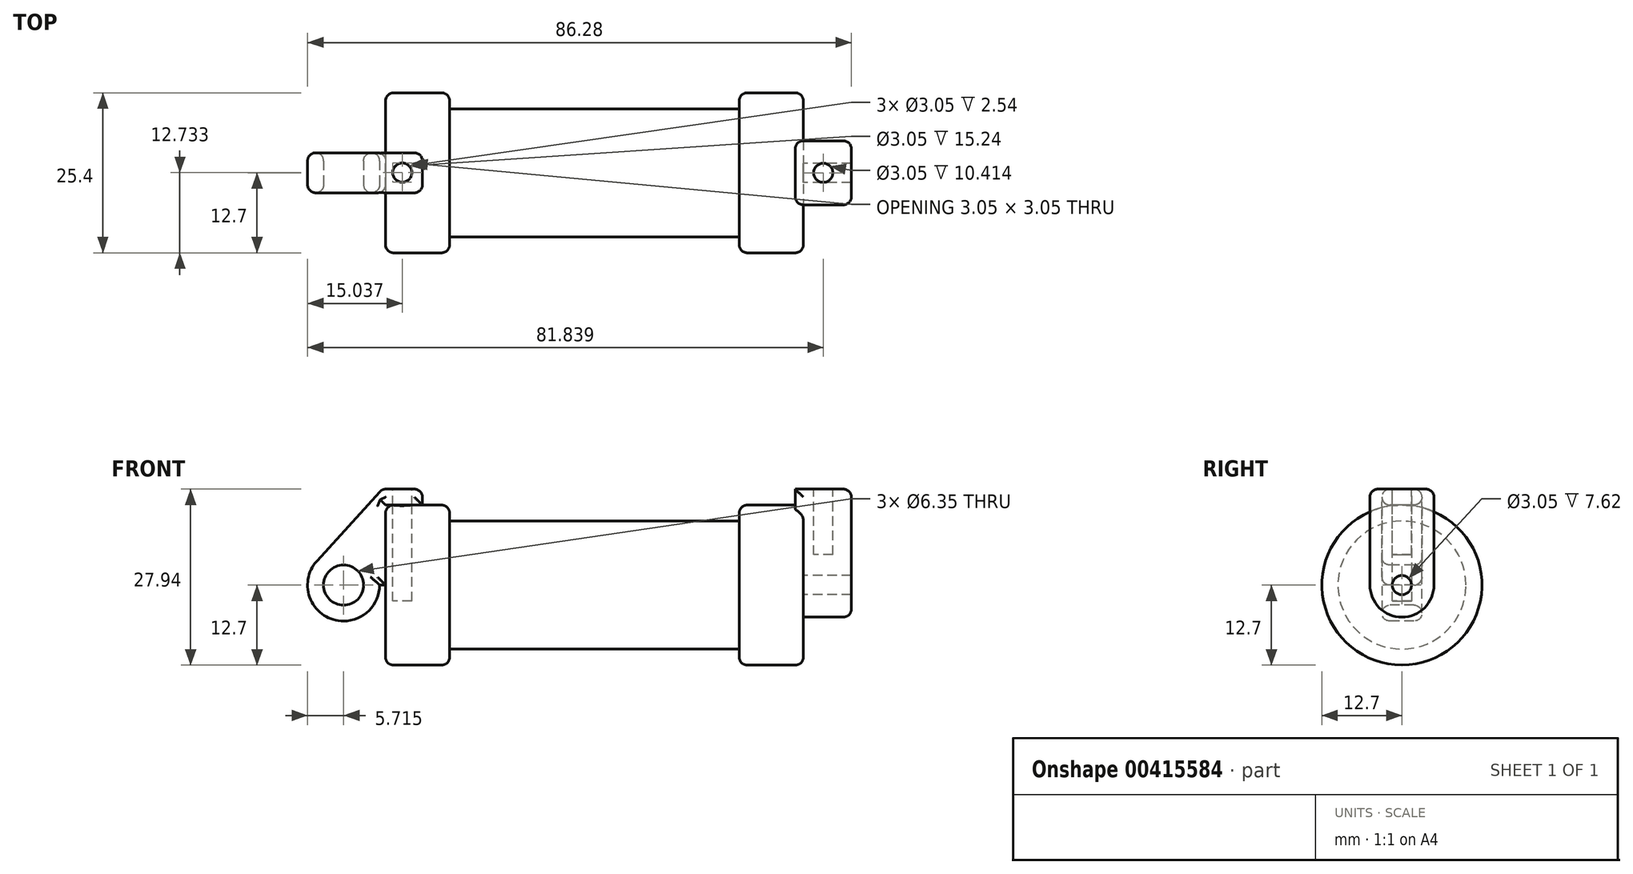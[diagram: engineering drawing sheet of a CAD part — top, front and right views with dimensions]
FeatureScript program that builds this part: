
annotation { "Feature Type Name" : "Feature", "Feature Type Description" : "" }
export const myFeature = defineFeature(function(context is Context, id is Id, definition is map)
    precondition{}
    {
        {
            var Q0;
            Q0=qCreatedBy(makeId("Front.planeOp"),FACE);
            var sketch = newSketch(context, id + "F0", { "sketchPlane" : qUnion([Q0])});
            skLineSegment(sketch, "E0", {"start": v(0, 0) * mm, "end": v(0, 12.7) * mm});
            skLineSegment(sketch, "E1", {"start": v(0, 12.7) * mm, "end": v(10.16, 12.7) * mm});
            skLineSegment(sketch, "E2", {"start": v(10.16, 12.7) * mm, "end": v(10.16, 10.16) * mm});
            skLineSegment(sketch, "E3", {"start": v(10.16, 10.16) * mm, "end": v(56.13, 10.16) * mm});
            skLineSegment(sketch, "E4", {"start": v(56.13, 10.16) * mm, "end": v(56.13, 12.7) * mm});
            skLineSegment(sketch, "E5", {"start": v(56.13, 12.7) * mm, "end": v(66.3, 12.7) * mm});
            skLineSegment(sketch, "E6", {"start": v(66.3, 12.7) * mm, "end": v(66.3, 0) * mm});
            skLineSegment(sketch, "E7", {"start": v(66.3, 0) * mm, "end": v(0, 0) * mm});
            skLineSegment(sketch, "E8", {"start": v(5.84, 15.24) * mm, "end": v(-0.5, 15.24) * mm});
            skLineSegment(sketch, "E9", {"start": v(-0.5, 15.24) * mm, "end": v(-10.88, 3.85) * mm});
            skLineSegment(sketch, "E10", {"start": v(0, 0) * mm, "end": v(-6.65, 0) * mm});
            skCircle(sketch, "E11", {"center": v(-6.65, 0) * mm, "radius": 5.72 * mm});
            skCircle(sketch, "E12", {"center": v(-6.65, 0) * mm, "radius": 3.18 * mm});
            skLineSegment(sketch, "E13", {"start": v(5.84, -9.4) * mm, "end": v(-8.18, -5.5) * mm});
            skLineSegment(sketch, "E14", {"start": v(5.84, 15.24) * mm, "end": v(5.84, 12.7) * mm});
            skSolve(sketch);
        }
        {
            var Q0;
            {var subQ3=sQuery(id+"F0.wireOp",EDGE,"E0");Q0=makeQuery(id+"F0.imprint","IMPRINT",FACE,{"disambiguationData":[TD([[makeQuery(id+"F0.imprint","IMPRINT",EDGE,{"derivedFrom":subQ3}),-1.0]])]});}
            var Q1;
            Q1=sQuery(id+"F0.wireOp",EDGE,"E7");
            revolve(context, id + "F1", {"entities" : qUnion([Q0]), "axis" : qUnion([Q1]), "revolveType" : RevolveType.FULL});
        }
        {
            var Q0;
            {var subQ5=sQuery(id+"F0.wireOp",EDGE,"E12");Q0=makeQuery(id+"F0.imprint","IMPRINT",FACE,{"disambiguationData":[TD([[makeQuery(id+"F0.imprint","IMPRINT",EDGE,{"derivedFrom":subQ5}),-1.0]])]});}
            var Q1;
            {var subQ1=sQuery(id+"F0.wireOp",EDGE,"E0");Q1=makeQuery(id+"F0.imprint","IMPRINT",FACE,{"disambiguationData":[TD([[makeQuery(id+"F0.imprint","IMPRINT",EDGE,{"derivedFrom":subQ1}),1.0]])]});}
            extrude(context, id + "F2", {"entities" : qUnion([Q0, Q1]), "endBound" : BoundingType.SYMMETRIC, "oppositeDirection" : true, "depth" : 6.35 * mm});
        }
        {
            var Q0;
            Q0=makeQuery(id+"F1.opRevolve","SWEPT_FACE",FACE,{"disambiguationData":[OSD([sQuery(id+"F0.wireOp",EDGE,"E6")])]});
            var sketch = newSketch(context, id + "F3", { "sketchPlane" : qUnion([Q0])});
            skCircle(sketch, "E15", {"center": v(0, 0) * mm, "radius": 1.52 * mm});
            skCircle(sketch, "E16", {"center": v(0, 0) * mm, "radius": 5.08 * mm});
            skLineSegment(sketch, "E17", {"start": v(-5.08, 0) * mm, "end": v(-5.08, 15.24) * mm});
            skLineSegment(sketch, "E18", {"start": v(5.08, 0) * mm, "end": v(5.08, 15.24) * mm});
            skLineSegment(sketch, "E19", {"start": v(-5.08, 15.24) * mm, "end": v(5.08, 15.24) * mm});
            skSolve(sketch);
        }
        {
            var Q0;
            {var subQ0=sQuery(id+"F3.wireOp",EDGE,"E19");Q0=makeQuery(id+"F3.imprint","IMPRINT",FACE,{"disambiguationData":[TD([[makeQuery(id+"F3.imprint","IMPRINT",EDGE,{"derivedFrom":subQ0}),-1.0]])]});}
            extrude(context, id + "F4", {"entities" : qUnion([Q0]), "operationType" : NewBodyOperationType.ADD, "oppositeDirection" : true, "depth" : 1.27 * mm});
        }
        {
            var Q0;
            {var subQ0=sQuery(id+"F3.wireOp",EDGE,"E17");var subQ1=sQuery(id+"F3.wireOp",EDGE,"E16");var subQ2=makeQuery(id+"F3.imprint","INTERSECT",VERTEX,{"derivedFrom":[subQ1,subQ0]});Q0=makeQuery(id+"F3.imprint","IMPRINT",FACE,{"disambiguationData":[TD([[makeQuery(id+"F3.imprint","IMPRINT",EDGE,{"disambiguationData":[TD([[subQ2,1.0]])],"derivedFrom":subQ1}),-1.0]])]});}
            var Q1;
            {var subQ0=sQuery(id+"F3.wireOp",EDGE,"E19");Q1=makeQuery(id+"F3.imprint","IMPRINT",FACE,{"disambiguationData":[TD([[makeQuery(id+"F3.imprint","IMPRINT",EDGE,{"derivedFrom":subQ0}),-1.0]])]});}
            var Q2;
            Q2=makeQuery(id+"F3.imprint","IMPRINT",FACE,{"disambiguationData":[TD([[makeQuery(id+"F3.imprint","IMPRINT",EDGE,{"derivedFrom":sQuery(id+"F3.wireOp",EDGE,"E15")}),-1.0]])]});
            extrude(context, id + "F5", {"entities" : qUnion([Q0, Q1, Q2]), "operationType" : NewBodyOperationType.ADD, "depth" : 7.62 * mm});
        }
        {
            var Q0;
            Q0=makeQuery(id+"F3.imprint","IMPRINT",FACE,{"disambiguationData":[TD([[makeQuery(id+"F3.imprint","IMPRINT",EDGE,{"derivedFrom":sQuery(id+"F3.wireOp",EDGE,"E15")}),1.0]])]});
            var Q1;
            Q1=makeQuery(id+"F1.opRevolve","SWEPT_FACE",FACE,{"disambiguationData":[OSD([sQuery(id+"F0.wireOp",EDGE,"E2")])]});
            extrude(context, id + "F6", {"entities" : qUnion([Q0]), "operationType" : NewBodyOperationType.ADD, "endBound" : BoundingType.UP_TO_SURFACE, "oppositeDirection" : true, "endBoundEntityFace" : qUnion([Q1]), "depth" : 64.77 * mm});
        }
        {
            var Q0;
            {var subQ0=sQuery(id+"F3.wireOp",EDGE,"E19");Q0=makeQuery(id+"F5.boolean.opBoolean","MERGE",FACE,{"derivedFrom":[makeQuery(id+"F4.opExtrude","SWEPT_FACE",FACE,{"disambiguationData":[OSD([subQ0])]}),makeQuery(id+"F5.opExtrude","SWEPT_FACE",FACE,{"disambiguationData":[OSD([subQ0])]})]});}
            var sketch = newSketch(context, id + "F7", { "sketchPlane" : qUnion([Q0])});
            skCircle(sketch, "E20", {"center": v(69.47, 0) * mm, "radius": 1.52 * mm});
            skLineSegment(sketch, "E21", {"start": v(69.47, 0) * mm, "end": v(73.91, 0) * mm, "construction": true});
            skLineSegment(sketch, "E22", {"start": v(69.47, 0) * mm, "end": v(69.47, 5.08) * mm, "construction": true});
            skSolve(sketch);
        }
        {
            var Q0;
            Q0=makeQuery(id+"F2.opExtrude","SWEPT_FACE",FACE,{"disambiguationData":[OSD([sQuery(id+"F0.wireOp",EDGE,"E8")])]});
            var sketch = newSketch(context, id + "F8", { "sketchPlane" : qUnion([Q0])});
            skCircle(sketch, "E23", {"center": v(2.67, 0.03) * mm, "radius": 1.52 * mm});
            skPoint(sketch, "E23.centerSnap0", {"position": v(2.67, 3.17) * mm});
            skSolve(sketch);
        }
        {
            var Q0;
            Q0=makeQuery(id+"F8.imprint","IMPRINT",FACE,{"disambiguationData":[TD([[makeQuery(id+"F8.imprint","IMPRINT",EDGE,{"derivedFrom":sQuery(id+"F8.wireOp",EDGE,"E23")}),1.0]])]});
            extrude(context, id + "F9", {"entities" : qUnion([Q0]), "operationType" : NewBodyOperationType.REMOVE, "oppositeDirection" : true, "depth" : 17.78 * mm});
        }
        {
            var Q0;
            Q0=makeQuery(id+"F7.imprint","IMPRINT",FACE,{"disambiguationData":[TD([[makeQuery(id+"F7.imprint","IMPRINT",EDGE,{"derivedFrom":sQuery(id+"F7.wireOp",EDGE,"E20")}),1.0]])]});
            extrude(context, id + "F10", {"entities" : qUnion([Q0]), "operationType" : NewBodyOperationType.REMOVE, "oppositeDirection" : true, "depth" : 10.4 * mm});
        }
        {
            var Q0;
            Q0=makeQuery(id+"F1.opRevolve","SWEPT_EDGE",EDGE,{"disambiguationData":[OSD([sQuery(id+"F0.wireOp",EDGE,"E5"),sQuery(id+"F0.wireOp",EDGE,"E6")])]});
            var Q1;
            Q1=makeQuery(id+"F1.opRevolve","SWEPT_EDGE",EDGE,{"disambiguationData":[OSD([sQuery(id+"F0.wireOp",EDGE,"E1"),sQuery(id+"F0.wireOp",EDGE,"E2")])]});
            var Q2;
            Q2=makeQuery(id+"F1.opRevolve","SWEPT_EDGE",EDGE,{"disambiguationData":[OSD([sQuery(id+"F0.wireOp",EDGE,"E0"),sQuery(id+"F0.wireOp",EDGE,"E1")])]});
            var Q3;
            Q3=makeQuery(id+"F1.opRevolve","SWEPT_EDGE",EDGE,{"disambiguationData":[OSD([sQuery(id+"F0.wireOp",EDGE,"E4"),sQuery(id+"F0.wireOp",EDGE,"E5")])]});
            fillet(context, id + "F11", {"entities" : qUnion([Q0, Q1, Q2, Q3]), "radius" : 1.27 * mm, "tangentPropagation" : true, "allowEdgeOverflow" : false});
        }
        {
            var Q0;
            Q0=makeQuery(id+"F5.opExtrude","CAP_EDGE",EDGE,{"disambiguationData":[OSD([sQuery(id+"F3.wireOp",EDGE,"E19")])],"isStart":false});
            var Q1;
            {var subQ0=sQuery(id+"F3.wireOp",EDGE,"E19");var subQ1=sQuery(id+"F3.wireOp",EDGE,"E17");Q1=makeQuery(id+"F5.boolean.opBoolean","MERGE",EDGE,{"derivedFrom":[makeQuery(id+"F4.opExtrude","SWEPT_EDGE",EDGE,{"disambiguationData":[OSD([subQ1,subQ0])]}),makeQuery(id+"F5.opExtrude","SWEPT_EDGE",EDGE,{"disambiguationData":[OSD([subQ1,subQ0])]})]});}
            var Q2;
            Q2=makeQuery(id+"F5.opExtrude","CAP_EDGE",EDGE,{"disambiguationData":[OSD([sQuery(id+"F3.wireOp",EDGE,"E18")])],"isStart":false});
            var Q3;
            Q3=makeQuery(id+"F4.opExtrude","CAP_EDGE",EDGE,{"disambiguationData":[OSD([sQuery(id+"F3.wireOp",EDGE,"E17")])],"isStart":false});
            var Q4;
            Q4=makeQuery(id+"F4.opExtrude","CAP_EDGE",EDGE,{"disambiguationData":[OSD([sQuery(id+"F3.wireOp",EDGE,"E18")])],"isStart":false});
            var Q5;
            {var subQ0=sQuery(id+"F3.wireOp",EDGE,"E19");var subQ1=sQuery(id+"F3.wireOp",EDGE,"E18");Q5=makeQuery(id+"F5.boolean.opBoolean","MERGE",EDGE,{"derivedFrom":[makeQuery(id+"F4.opExtrude","SWEPT_EDGE",EDGE,{"disambiguationData":[OSD([subQ1,subQ0])]}),makeQuery(id+"F5.opExtrude","SWEPT_EDGE",EDGE,{"disambiguationData":[OSD([subQ1,subQ0])]})]});}
            fillet(context, id + "F12", {"entities" : qUnion([Q0, Q1, Q2, Q3, Q4, Q5]), "radius" : 1.27 * mm, "tangentPropagation" : true, "allowEdgeOverflow" : false});
        }
        {
            var Q0;
            Q0=makeQuery(id+"F2.opExtrude","CAP_EDGE",EDGE,{"disambiguationData":[OSD([sQuery(id+"F0.wireOp",EDGE,"E8")])],"isStart":false});
            var Q1;
            Q1=makeQuery(id+"F2.opExtrude","SWEPT_EDGE",EDGE,{"disambiguationData":[OSD([sQuery(id+"F0.wireOp",EDGE,"E8"),sQuery(id+"F0.wireOp",EDGE,"E14")])]});
            var Q2;
            Q2=makeQuery(id+"F2.opExtrude","CAP_EDGE",EDGE,{"disambiguationData":[OSD([sQuery(id+"F0.wireOp",EDGE,"E8")])],"isStart":true});
            var Q3;
            Q3=makeQuery(id+"F2.opExtrude","SWEPT_EDGE",EDGE,{"disambiguationData":[OSD([sQuery(id+"F0.wireOp",EDGE,"E8"),sQuery(id+"F0.wireOp",EDGE,"E9")])]});
            var Q4;
            Q4=makeQuery(id+"F2.opExtrude","CAP_EDGE",EDGE,{"disambiguationData":[OSD([sQuery(id+"F0.wireOp",EDGE,"E9")])],"isStart":true});
            var Q5;
            Q5=makeQuery(id+"F2.opExtrude","CAP_EDGE",EDGE,{"disambiguationData":[OSD([sQuery(id+"F0.wireOp",EDGE,"E9")])],"isStart":false});
            var Q6;
            Q6=makeQuery(id+"F2.opExtrude","CAP_FACE",FACE,{"disambiguationData":[OSD([sQuery(id+"F0.wireOp",EDGE,"E0"),sQuery(id+"F0.wireOp",EDGE,"E1"),sQuery(id+"F0.wireOp",EDGE,"E8"),sQuery(id+"F0.wireOp",EDGE,"E9"),sQuery(id+"F0.wireOp",EDGE,"E10"),sQuery(id+"F0.wireOp",EDGE,"E11"),sQuery(id+"F0.wireOp",EDGE,"E12"),sQuery(id+"F0.wireOp",EDGE,"E14")])],"isStart":true});
            var Q7;
            Q7=makeQuery(id+"F2.opExtrude","CAP_FACE",FACE,{"disambiguationData":[OSD([sQuery(id+"F0.wireOp",EDGE,"E0"),sQuery(id+"F0.wireOp",EDGE,"E1"),sQuery(id+"F0.wireOp",EDGE,"E8"),sQuery(id+"F0.wireOp",EDGE,"E9"),sQuery(id+"F0.wireOp",EDGE,"E10"),sQuery(id+"F0.wireOp",EDGE,"E11"),sQuery(id+"F0.wireOp",EDGE,"E12"),sQuery(id+"F0.wireOp",EDGE,"E14")])],"isStart":false});
            fillet(context, id + "F13", {"entities" : qUnion([Q0, Q1, Q2, Q3, Q4, Q5, Q6, Q7]), "radius" : 1.27 * mm, "tangentPropagation" : true, "allowEdgeOverflow" : false});
        }
    });
